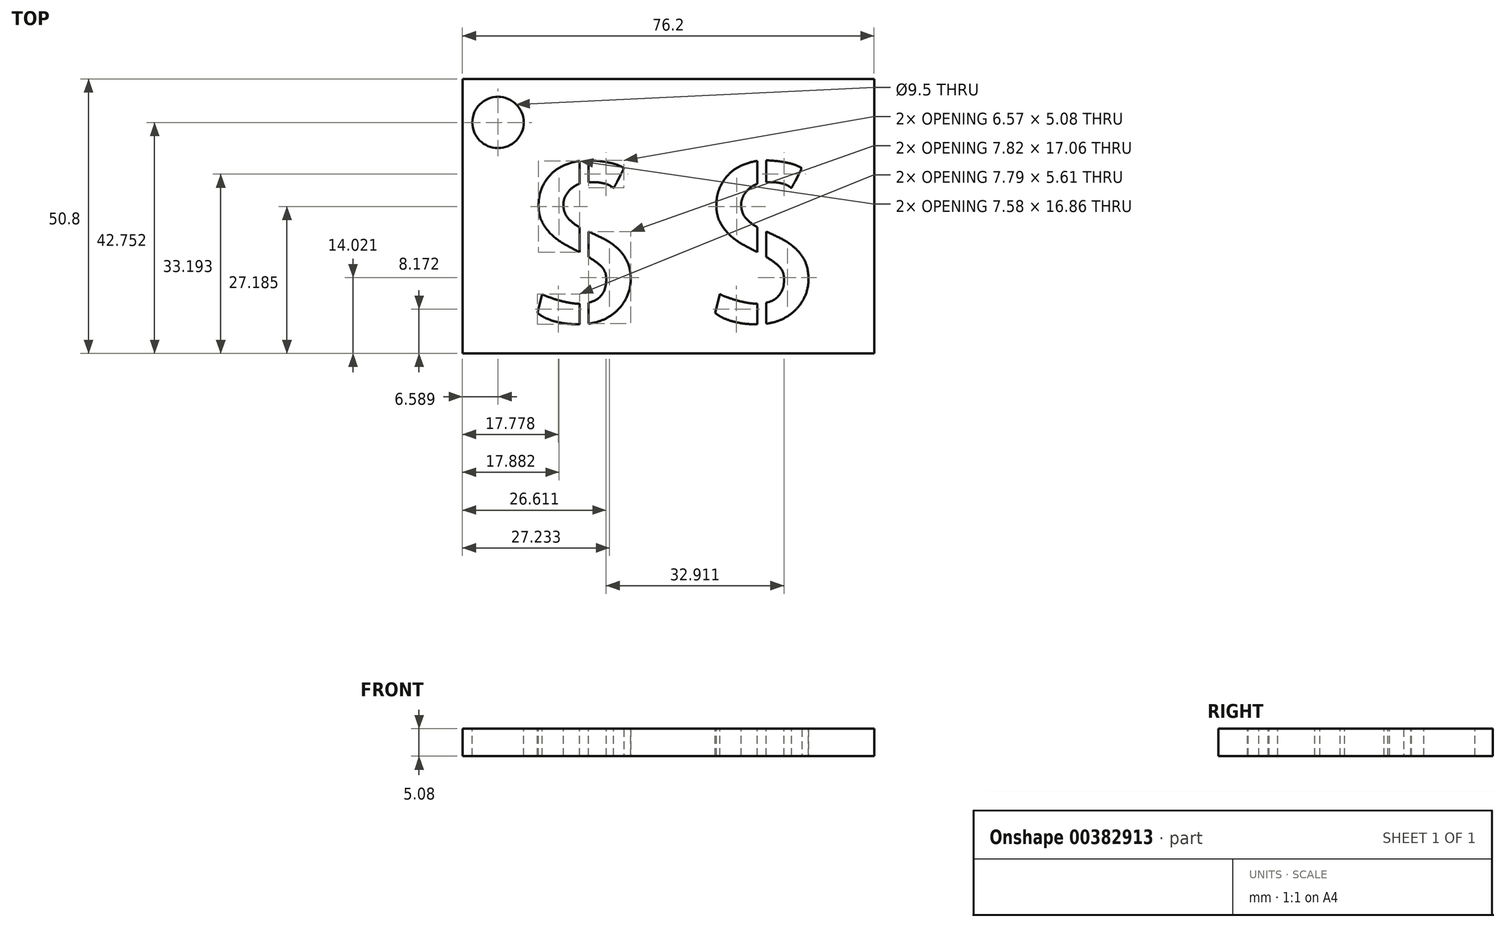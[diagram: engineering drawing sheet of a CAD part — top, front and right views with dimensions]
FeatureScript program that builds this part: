
annotation { "Feature Type Name" : "Feature", "Feature Type Description" : "" }
export const myFeature = defineFeature(function(context is Context, id is Id, definition is map)
    precondition{}
    {
        {
            var Q0;
            Q0=qCreatedBy(makeId("Top.planeOp"),FACE);
            var sketch = newSketch(context, id + "F0", { "sketchPlane" : qUnion([Q0])});
            skLineSegment(sketch, "E0.bottom", {"start": v(-37.96, 14.67) * mm, "end": v(38.24, 14.67) * mm});
            skLineSegment(sketch, "E0.top", {"start": v(-37.96, -36.13) * mm, "end": v(38.24, -36.13) * mm});
            skLineSegment(sketch, "E0.left", {"start": v(-37.96, 14.67) * mm, "end": v(-37.96, -36.13) * mm});
            skLineSegment(sketch, "E0.right", {"start": v(38.24, 14.67) * mm, "end": v(38.24, -36.13) * mm});
            skSolve(sketch);
        }
        {
            var Q0;
            Q0=makeQuery(id+"F0.imprint","IMPRINT",FACE,{"disambiguationData":[TD([[makeQuery(id+"F0.imprint","IMPRINT",EDGE,{"derivedFrom":sQuery(id+"F0.wireOp",EDGE,"E0.bottom")}),-1.0]])]});
            extrude(context, id + "F1", {"entities" : qUnion([Q0]), "depth" : 5.08 * mm});
        }
        {
            var Q0;
            Q0=makeQuery(id+"F1.opExtrude","CAP_FACE",FACE,{"disambiguationData":[OSD([sQuery(id+"F0.wireOp",EDGE,"E0.bottom"),sQuery(id+"F0.wireOp",EDGE,"E0.top"),sQuery(id+"F0.wireOp",EDGE,"E0.left"),sQuery(id+"F0.wireOp",EDGE,"E0.right")])],"isStart":false});
            var sketch = newSketch(context, id + "F2", { "sketchPlane" : qUnion([Q0])});
            skCircle(sketch, "E1", {"center": v(-31.37, 6.62) * mm, "radius": 4.75 * mm});
            skSolve(sketch);
        }
        {
            var Q0;
            Q0=makeQuery(id+"F2.imprint","IMPRINT",FACE,{"disambiguationData":[TD([[makeQuery(id+"F2.imprint","IMPRINT",EDGE,{"derivedFrom":sQuery(id+"F2.wireOp",EDGE,"E1")}),-1.0]])]});
            var sketch = newSketch(context, id + "F3", { "sketchPlane" : qUnion([Q0])});
            skText(sketch, "E2", { "text": "S S", "fontName": "AllertaStencil-Regular.ttf"});
            const initialGuessF3  = {"E2": [-0.02734, -0.0306, 1, 0, 0.02973]};
            skSetInitialGuess(sketch, initialGuessF3);
            skSolve(sketch);
        }
        {
            var Q0;
            Q0=makeQuery(id+"F2.imprint","IMPRINT",FACE,{"disambiguationData":[TD([[makeQuery(id+"F2.imprint","IMPRINT",EDGE,{"derivedFrom":sQuery(id+"F2.wireOp",EDGE,"E1")}),1.0]])]});
            extrude(context, id + "F4", {"entities" : qUnion([Q0]), "operationType" : NewBodyOperationType.REMOVE, "oppositeDirection" : true, "depth" : 25.4 * mm});
        }
        {
            var Q0;
            Q0 = qSketchRegion(id + "F3", true);
            extrude(context, id + "F5", {"entities" : qUnion([Q0]), "operationType" : NewBodyOperationType.REMOVE, "oppositeDirection" : true, "depth" : 25.4 * mm});
        }
    });
